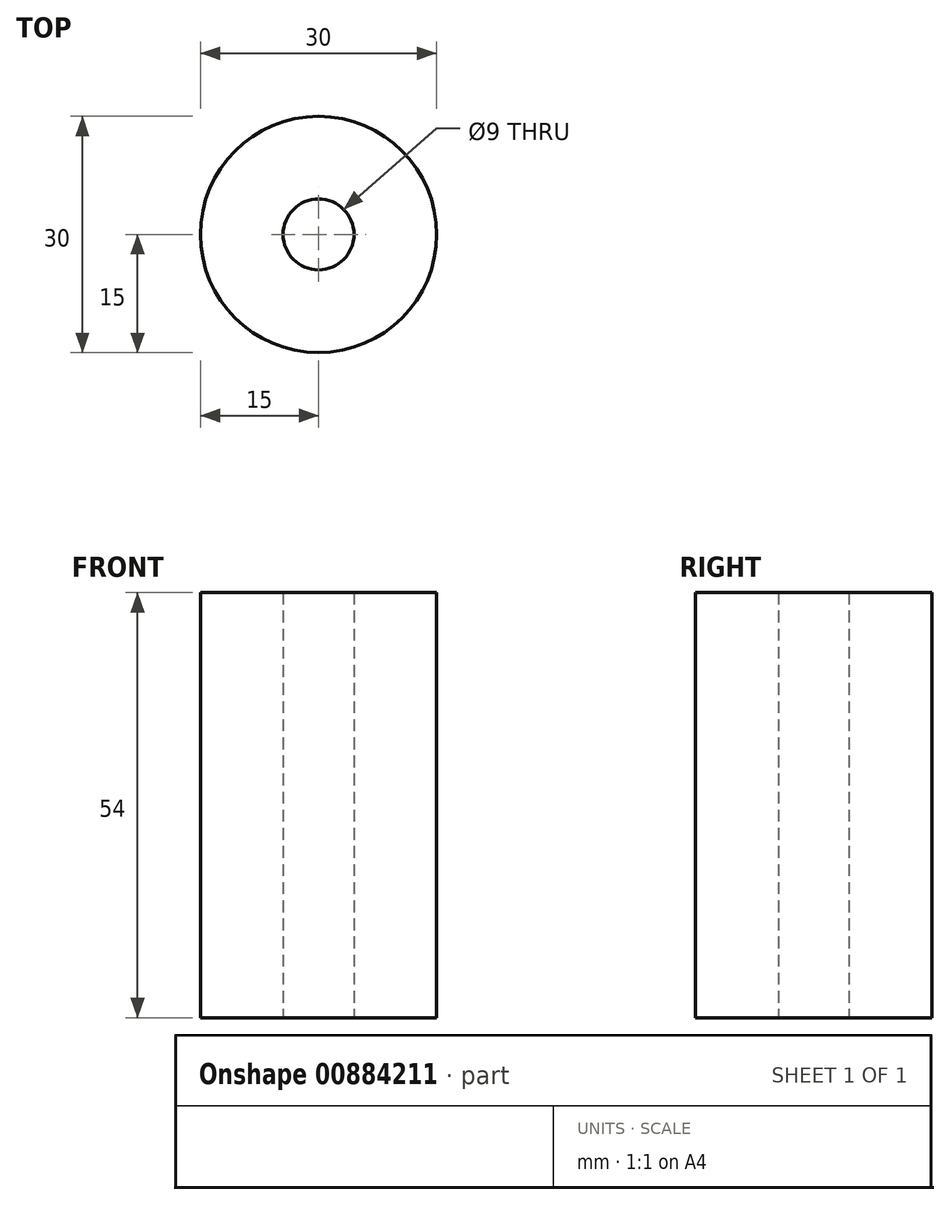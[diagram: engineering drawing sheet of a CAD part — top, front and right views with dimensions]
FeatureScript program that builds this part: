
annotation { "Feature Type Name" : "Feature", "Feature Type Description" : "" }
export const myFeature = defineFeature(function(context is Context, id is Id, definition is map)
    precondition{}
    {
        {
            var Q0;
            Q0=qCreatedBy(makeId("Top.planeOp"),FACE);
            var sketch = newSketch(context, id + "F0", { "sketchPlane" : qUnion([Q0])});
            skCircle(sketch, "E0", {"center": v(0, 0) * mm, "radius": 15 * mm});
            skCircle(sketch, "E1", {"center": v(0, 0) * mm, "radius": 4.5 * mm});
            skSolve(sketch);
        }
        {
            var Q0;
            Q0=makeQuery(id+"F0.imprint","IMPRINT",FACE,{"disambiguationData":[TD([[makeQuery(id+"F0.imprint","IMPRINT",EDGE,{"derivedFrom":sQuery(id+"F0.wireOp",EDGE,"E0")}),1.0]])]});
            extrude(context, id + "F1", {"entities" : qUnion([Q0]), "depth" : 54 * mm, "offsetDistance" : 25 * mm});
        }
    });
